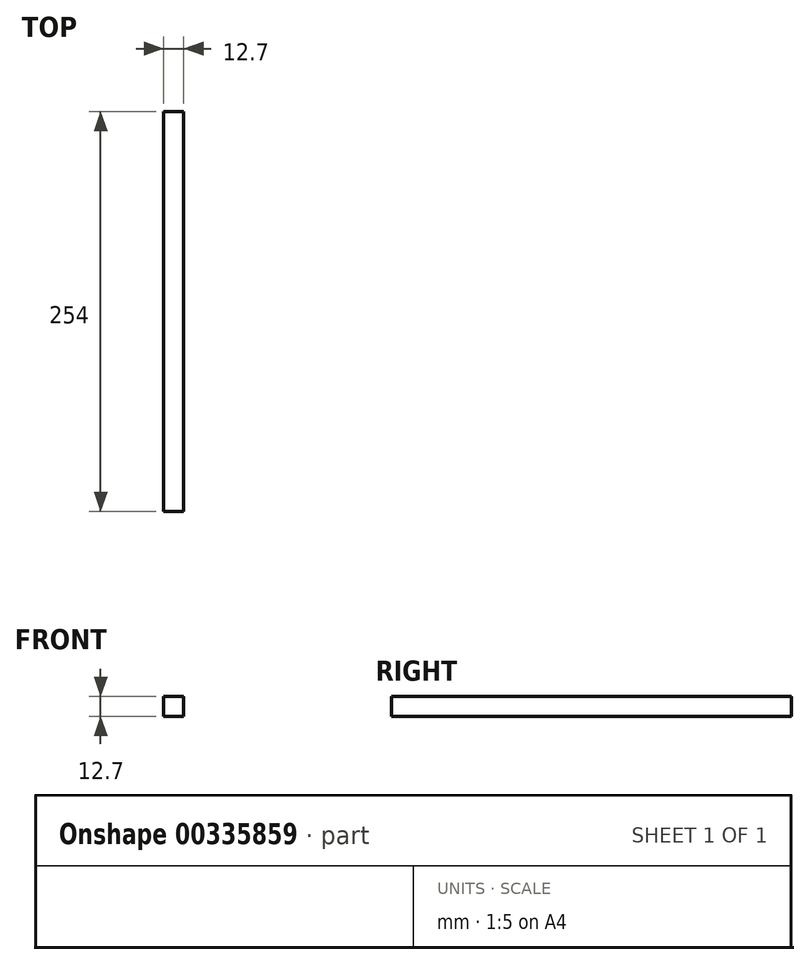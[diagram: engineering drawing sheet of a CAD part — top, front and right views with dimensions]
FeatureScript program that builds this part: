
annotation { "Feature Type Name" : "Feature", "Feature Type Description" : "" }
export const myFeature = defineFeature(function(context is Context, id is Id, definition is map)
    precondition{}
    {
        {
            var Q0;
            Q0=qCreatedBy(makeId("Front.planeOp"),FACE);
            var sketch = newSketch(context, id + "F0", { "sketchPlane" : qUnion([Q0])});
            skLineSegment(sketch, "E0.bottom", {"start": v(0, 12.7) * mm, "end": v(12.7, 12.7) * mm});
            skLineSegment(sketch, "E0.top", {"start": v(0, 0) * mm, "end": v(12.7, 0) * mm});
            skLineSegment(sketch, "E0.left", {"start": v(0, 12.7) * mm, "end": v(0, 0) * mm});
            skLineSegment(sketch, "E0.right", {"start": v(12.7, 12.7) * mm, "end": v(12.7, 0) * mm});
            skSolve(sketch);
        }
        {
            var Q0;
            Q0 = qSketchRegion(id + "F0", true);
            extrude(context, id + "F1", {"entities" : qUnion([Q0]), "depth" : 254 * mm});
        }
    });
